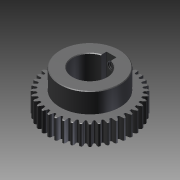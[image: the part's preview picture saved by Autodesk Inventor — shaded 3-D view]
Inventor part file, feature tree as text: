
AUTODESK INVENTOR PART (.ipt)
format: ipt  version: 2011 SP1 (Build 150282100, 282)  size: 1,227,776 bytes
history: native  units: mm
features: other x21, sketch x5, revolve x4, extrude x2, hole x1, thread x1
ambient origin geometry x8: Origin, YZ Plane, XZ Plane, XY Plane, X Axis, Y Axis, Z Axis, Center Point
bodies: Solid1 (feature_tree)
feature tree (34):
  revolve  "Revolution1"  [1 undecoded]
  extrude  "Extrusion1"  TaperAngle=360.0deg  [1 undecoded]
  hole  "Hole1"  [1 undecoded]
  revolve  "Revolution2"  [1 undecoded]
  revolve  "Revolution3"  [1 undecoded]
  extrude  "Extrusion2"  [1 undecoded]
  revolve  "Revolution4"  [1 undecoded]
  thread  "Thread1"  [1 undecoded]
  other  "b_XY"
  other  "b_YZ"
  other  "b_ZX"
  other  "b_X"
  other  "b_Y"
  other  "b_Z"
  other  "b_Center"
  other  "screw_XY"
  other  "screw_YZ"
  other  "screw_ZX"
  other  "screw_X"
  other  "screw_Y"
  other  "screw_Z"
  other  "screw_Center"
  other  "turn_around_XY"
  other  "turn_around_YZ"
  other  "turn_around_ZX"
  other  "turn_around_X"
  other  "turn_around_Y"
  other  "turn_around_Z"
  other  "turn_around_Center"
  sketch  "Sketch_2"  dims[d0=360.0deg d1=10.0mm d2=0.0mm]
  sketch  "Sketch_3"  dims[d3=17.0mm d4=6.0mm d5=4.0mm d6=2.0mm d7=90.0deg d8=20.0mm d9=0.0mm d10=360.0deg]
  sketch  "Sketch3"  dims[d11=360.0deg d12=20.0mm d13=0.0mm]
  sketch  "Sketch_31"  dims[d17=0.0mm d18=0.0mm]
  sketch  "Sketch_4"  dims[d14=360.0deg d15=3.767mm d16=0.0mm]
note: 8 required parameter values undecoded (feature->parameter linkage not recoverable at this tier; creation-order binding heuristic only, values carry confidence <= 0.55)